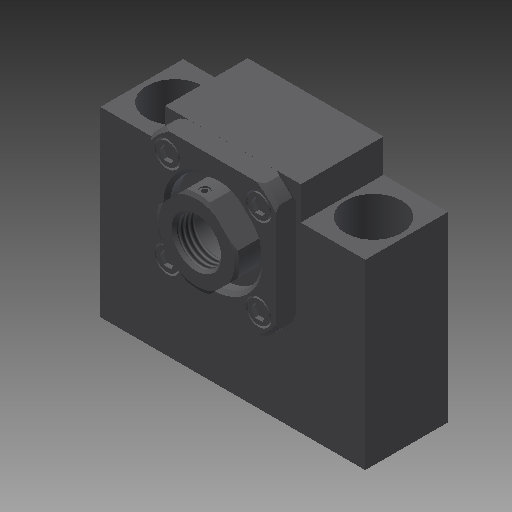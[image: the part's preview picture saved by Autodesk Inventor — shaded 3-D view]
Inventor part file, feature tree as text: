
AUTODESK INVENTOR PART (.ipt)
format: ipt  version: 2018 (Build 220112000, 112)  size: 391,168 bytes
history: native  units: mm
features: sketch x24, other x14, revolve x12, extrude x10, pattern_linear x3, hole x2, thread x1
ambient origin geometry x8: Origin, YZ Plane, XZ Plane, XY Plane, X Axis, Y Axis, Z Axis, Center Point
bodies: Solid1 (feature_tree)
feature tree (66):
  extrude  "Extrusion1"  Depth=2.5mm TaperAngle=0.0deg
  extrude  "Extrusion2"  Depth=8.5mm TaperAngle=0.0deg
  revolve  "Revolution1"  Angle=360.0deg
  extrude  "Extrusion3"  TaperAngle=360.0deg  [1 undecoded]
  extrude  "Extrusion4"  TaperAngle=360.0deg  [1 undecoded]
  revolve  "Revolution2"  [1 undecoded]
  hole  "Hole5"  [1 undecoded]
  revolve  "Revolution3"  [1 undecoded]
  thread  "Thread1"  [1 undecoded]
  revolve  "Revolution4"  [1 undecoded]
  revolve  "Revolution5"  Angle=360.0deg
  pattern_linear  "Rectangular Pattern1"  Count1=8  [1 undecoded]
  revolve  "Revolution6"  [1 undecoded]
  pattern_linear  "Rectangular Pattern2"  Spacing1=11.0mm  [1 undecoded]
  extrude  "Extrusion5"  Depth=25.0mm
  pattern_linear  "Rectangular Pattern3"  Count1=8  [1 undecoded]
  revolve  "Revolution7"  [1 undecoded]
  revolve  "Revolution8"  [1 undecoded]
  extrude  "Extrusion6"  [1 undecoded]
  revolve  "Revolution9"  [1 undecoded]
  revolve  "Revolution10"  [1 undecoded]
  extrude  "Extrusion7"  [1 undecoded]
  extrude  "Extrusion8"  [1 undecoded]
  revolve  "Revolution11"  [1 undecoded]
  revolve  "Revolution12"  [1 undecoded]
  extrude  "Extrusion9"  [1 undecoded]
  other  "unit_XY"
  other  "unit_YZ"
  other  "unit_ZX"
  other  "unit_X"
  other  "unit_Y"
  other  "unit_Z"
  other  "unit_Center"
  other  "unit_collar_XY"
  other  "unit_collar_YZ"
  other  "unit_collar_ZX"
  other  "unit_collar_X"
  other  "unit_collar_Y"
  other  "unit_collar_Z"
  other  "unit_collar_Center"
  hole  "Hole6"  [1 undecoded]
  extrude  "Extrusion11"  [1 undecoded]
  sketch  "Sketch_1"  dims[d0=25.0mm d1=0.0mm d30=2.5mm d31=0.0mm]
  sketch  "Sketch_10"  dims[d32=360.0deg d33=8.5mm d34=0.0mm]
  sketch  "Sketch_13"  dims[d49=360.0deg d50=20.0mm d52=27.577164mm d53=20.0mm d55=27.577164mm]
  sketch  "Sketch_11"  dims[d35=3.5mm d36=0.0mm d37=360.0deg]
  sketch  "Sketch_12"  dims[d46=6.876mm d47=0.0mm d48=360.0deg]
  sketch  "Sketch_14"  dims[d56=360.0deg d57=20.0mm d59=27.577164mm d60=20.0mm d62=27.577164mm]
  sketch  "Sketch11"  dims[d38=15.0mm d39=6.0mm d40=19.5mm d41=6.0mm d42=90.0deg d43=30.0mm d44=0.0mm d45=360.0deg]
  sketch  "Sketch_16"  dims[d63=1.2mm d64=0.0mm d65=20.0mm d67=27.577164mm d68=20.0mm d70=27.577164mm d71=360.0deg]
  sketch  "Sketch_17"  dims[d72=360.0deg d73=1.2mm d74=0.0mm]
  sketch  "Sketch_18"  dims[d75=360.0deg d76=360.0deg]
  sketch  "Sketch_20"  dims[d77=16.0mm d78=0.0mm]
  sketch  "Sketch_22"  dims[d79=6.0mm d80=0.0mm]
  sketch  "Sketch_24"  dims[d81=360.0deg]
  sketch  "Sketch_25"  dims[d82=360.0deg]
  sketch  "Sketch_26"  dims[d83=0.01mm d84=0.0mm]
  sketch  "Sketch_28"  dims[d90=19.5mm d91=30.0mm]
  sketch  "Sketch_29"  dims[d92=19.5mm]
  sketch  "Sketch_33"  dims[d98=10.0mm d99=11.0mm d100=6.0mm d101=17.0mm d102=15.0mm d103=90.0deg d104=8.0mm d105=20.594885mm d108=11.0mm d109=11.0mm d110=80.0mm d111=25.0mm d112=25.0mm d113=0.0mm]
  sketch  "Sketch_27"  dims[d85=0.0mm]
  sketch  "Sketch_30"  dims[d93=10.0mm]
  sketch  "Sketch_31"  dims[d95=10.0mm]
  sketch  "Sketch_32"  dims[d97=10.0mm]
  sketch  "Sketch27"  dims[d86=0.0mm d89=80.0mm]
  sketch  "Sketch30"  dims[d94=41.0mm]
note: 23 required parameter values undecoded (feature->parameter linkage not recoverable at this tier; creation-order binding heuristic only, values carry confidence <= 0.55)